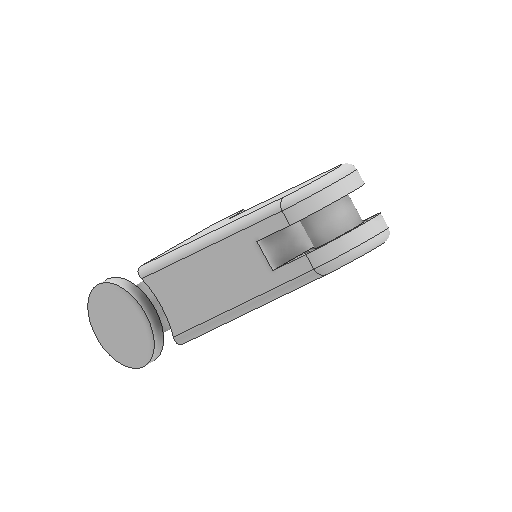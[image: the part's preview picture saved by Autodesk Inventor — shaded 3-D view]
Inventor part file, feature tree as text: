
AUTODESK INVENTOR PART (.ipt)
format: ipt  version: 2022 (Build 260153000, 153)  size: 165,376 bytes
history: native  units: mm
features: sketch x6, other x3
ambient origin geometry x8: Origin, YZ Plane, XZ Plane, XY Plane, X Axis, Y Axis, Z Axis, Center Point
bodies: Solid1 (feature_tree)
feature tree (9):
  other  "Upper Arm.ipt"
  other  "Solid1::Upper Arm.ipt"
  other  "TaggingFeature1"
  sketch  "Sketch1"  dims[d0=10.0mm]
  sketch  "Sketch2"
  sketch  "Sketch3"
  sketch  "Sketch4"
  sketch  "Sketch5"
  sketch  "Sketch6"
